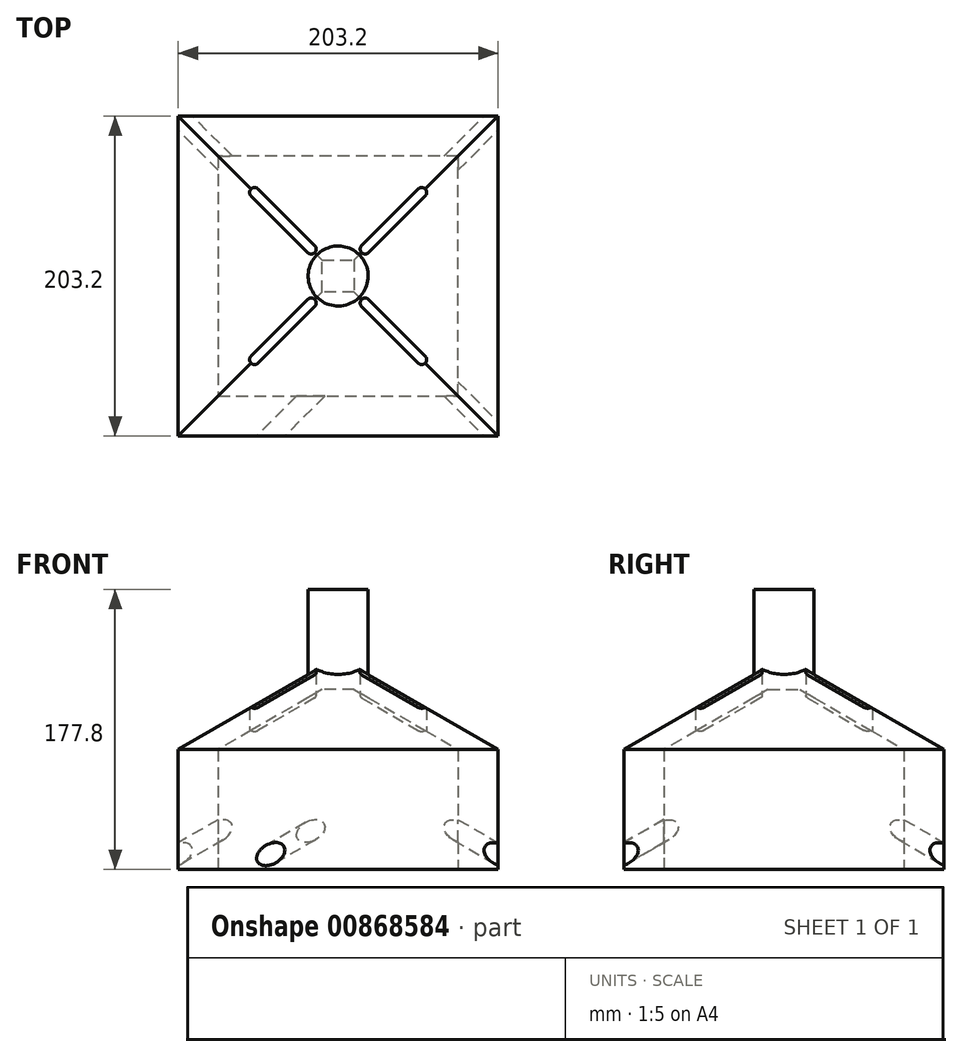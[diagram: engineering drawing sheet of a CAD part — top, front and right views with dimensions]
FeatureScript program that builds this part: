
annotation { "Feature Type Name" : "Feature", "Feature Type Description" : "" }
export const myFeature = defineFeature(function(context is Context, id is Id, definition is map)
    precondition{}
    {
        {
            var Q0;
            Q0=qCreatedBy(makeId("Top.planeOp"),FACE);
            var sketch = newSketch(context, id + "F0", { "sketchPlane" : qUnion([Q0])});
            skLineSegment(sketch, "E0.bottom", {"start": v(101.6, -101.6) * mm, "end": v(-101.6, -101.6) * mm});
            skLineSegment(sketch, "E0.top", {"start": v(101.6, 101.6) * mm, "end": v(-101.6, 101.6) * mm});
            skLineSegment(sketch, "E0.left", {"start": v(101.6, -101.6) * mm, "end": v(101.6, 101.6) * mm});
            skLineSegment(sketch, "E0.right", {"start": v(-101.6, -101.6) * mm, "end": v(-101.6, 101.6) * mm});
            skSolve(sketch);
        }
        {
            var Q0;
            Q0 = qSketchRegion(id + "F0", true);
            extrude(context, id + "F1", {"entities" : qUnion([Q0]), "depth" : 127 * mm, "offsetDistance" : 25.4 * mm});
        }
        {
            var Q0;
            Q0=makeQuery(id+"F0.imprint","IMPRINT",FACE,{"disambiguationData":[TD([[makeQuery(id+"F0.imprint","IMPRINT",EDGE,{"derivedFrom":sQuery(id+"F0.wireOp",EDGE,"E0.bottom")}),-1.0]])]});
            var sketch = newSketch(context, id + "F2", { "sketchPlane" : qUnion([Q0])});
            skLineSegment(sketch, "E1.0", {"start": v(76.2, -76.2) * mm, "end": v(76.2, 76.2) * mm});
            skLineSegment(sketch, "E1.1", {"start": v(-76.2, -76.2) * mm, "end": v(76.2, -76.2) * mm});
            skLineSegment(sketch, "E1.2", {"start": v(-76.2, 76.2) * mm, "end": v(-76.2, -76.2) * mm});
            skLineSegment(sketch, "E1.3", {"start": v(76.2, 76.2) * mm, "end": v(-76.2, 76.2) * mm});
            skSolve(sketch);
        }
        {
            var Q0;
            Q0 = qSketchRegion(id + "F2", true);
            extrude(context, id + "F3", {"entities" : qUnion([Q0]), "operationType" : NewBodyOperationType.REMOVE, "depth" : 76.2 * mm, "offsetDistance" : 25.4 * mm});
        }
        {
            var Q0;
            Q0=makeQuery(id+"F3.boolean.opBoolean","COPY",FACE,{"derivedFrom":makeQuery(id+"F3.opExtrude","CAP_FACE",FACE,{"disambiguationData":[OSD([sQuery(id+"F2.wireOp",EDGE,"E1.0"),sQuery(id+"F2.wireOp",EDGE,"E1.1"),sQuery(id+"F2.wireOp",EDGE,"E1.2"),sQuery(id+"F2.wireOp",EDGE,"E1.3")])],"isStart":false})});
            var sketch = newSketch(context, id + "F4", { "sketchPlane" : qUnion([Q0])});
            skLineSegment(sketch, "E2.0.0", {"start": v(76.2, -76.2) * mm, "end": v(76.2, 76.2) * mm});
            skLineSegment(sketch, "E2.0.1", {"start": v(76.2, 76.2) * mm, "end": v(-76.2, 76.2) * mm});
            skLineSegment(sketch, "E2.0.2", {"start": v(-76.2, 76.2) * mm, "end": v(-76.2, -76.2) * mm});
            skLineSegment(sketch, "E2.0.3", {"start": v(-76.2, -76.2) * mm, "end": v(76.2, -76.2) * mm});
            skSolve(sketch);
        }
        {
            var Q0;
            Q0 = qSketchRegion(id + "F4", true);
            extrude(context, id + "F5", {"entities" : qUnion([Q0]), "operationType" : NewBodyOperationType.REMOVE, "oppositeDirection" : true, "depth" : 101.6 * mm, "offsetDistance" : 25.4 * mm, "hasDraft" : true, "draftAngle" : 60 * degree, "draftPullDirection" : true});
        }
        {
            var Q0;
            Q0=makeQuery(id+"F1.opExtrude","CAP_EDGE",EDGE,{"disambiguationData":[OSD([sQuery(id+"F0.wireOp",EDGE,"E0.right")])],"isStart":false});
            var Q1;
            Q1=makeQuery(id+"F1.opExtrude","CAP_EDGE",EDGE,{"disambiguationData":[OSD([sQuery(id+"F0.wireOp",EDGE,"E0.top")])],"isStart":false});
            var Q2;
            Q2=makeQuery(id+"F1.opExtrude","CAP_EDGE",EDGE,{"disambiguationData":[OSD([sQuery(id+"F0.wireOp",EDGE,"E0.left")])],"isStart":false});
            var Q3;
            Q3=makeQuery(id+"F1.opExtrude","CAP_EDGE",EDGE,{"disambiguationData":[OSD([sQuery(id+"F0.wireOp",EDGE,"E0.bottom")])],"isStart":false});
            chamfer(context, id + "F6", {"entities" : qUnion([Q0, Q1, Q2, Q3]), "chamferType" : ChamferType.OFFSET_ANGLE, "width" : 50.8 * mm, "oppositeDirection" : false, "angle" : 60 * degree, "tangentPropagation" : true});
        }
        {
            var Q0;
            Q0=qCreatedBy(makeId("Top.planeOp"),FACE);
            var sketch = newSketch(context, id + "F7", { "sketchPlane" : qUnion([Q0])});
            skArc(sketch, "E3", {"start": v(-55.32, -50.82) * mm, "mid": v(-55.32, -55.32) * mm, "end": v(-50.82, -55.32) * mm});
            skArc(sketch, "E4", {"start": v(-14.9, -19.4) * mm, "mid": v(-14.9, -14.9) * mm, "end": v(-19.4, -14.9) * mm});
            skLineSegment(sketch, "E5", {"start": v(-50.82, -55.32) * mm, "end": v(-14.9, -19.4) * mm});
            skLineSegment(sketch, "E6", {"start": v(-55.32, -50.82) * mm, "end": v(-19.4, -14.9) * mm});
            skLineSegment(sketch, "E7", {"start": v(-55.32, -50.82) * mm, "end": v(-43.18, -62.96) * mm, "construction": true});
            skLineSegment(sketch, "E8", {"start": v(-25.58, -8.72) * mm, "end": v(-3.68, -30.62) * mm, "construction": true});
            skArc(sketch, "E9.1.0", {"start": v(-19.4, 14.9) * mm, "mid": v(-14.9, 14.9) * mm, "end": v(-14.9, 19.4) * mm});
            skLineSegment(sketch, "E9.1.1", {"start": v(-55.32, 50.82) * mm, "end": v(-19.4, 14.9) * mm});
            skLineSegment(sketch, "E9.1.2", {"start": v(-50.82, 55.32) * mm, "end": v(-14.9, 19.4) * mm});
            skArc(sketch, "E9.1.3", {"start": v(-50.82, 55.32) * mm, "mid": v(-55.32, 55.32) * mm, "end": v(-55.32, 50.82) * mm});
            skArc(sketch, "E9.2.0", {"start": v(14.9, 19.4) * mm, "mid": v(14.9, 14.9) * mm, "end": v(19.4, 14.9) * mm});
            skLineSegment(sketch, "E9.2.1", {"start": v(50.82, 55.32) * mm, "end": v(14.9, 19.4) * mm});
            skLineSegment(sketch, "E9.2.2", {"start": v(55.32, 50.82) * mm, "end": v(19.4, 14.9) * mm});
            skArc(sketch, "E9.2.3", {"start": v(55.32, 50.82) * mm, "mid": v(55.32, 55.32) * mm, "end": v(50.82, 55.32) * mm});
            skArc(sketch, "E9.3.0", {"start": v(19.4, -14.9) * mm, "mid": v(14.9, -14.9) * mm, "end": v(14.9, -19.4) * mm});
            skLineSegment(sketch, "E9.3.1", {"start": v(55.32, -50.82) * mm, "end": v(19.4, -14.9) * mm});
            skLineSegment(sketch, "E9.3.2", {"start": v(50.82, -55.32) * mm, "end": v(14.9, -19.4) * mm});
            skArc(sketch, "E9.3.3", {"start": v(50.82, -55.32) * mm, "mid": v(55.32, -55.32) * mm, "end": v(55.32, -50.82) * mm});
            skPoint(sketch, "E9.center", {"position": v(0, 0) * mm});
            skLineSegment(sketch, "E9.anchor1", {"start": v(0, 0) * mm, "end": v(-14.9, -19.4) * mm, "construction": true});
            skLineSegment(sketch, "E9.anchor2", {"start": v(0, 0) * mm, "end": v(19.4, -14.9) * mm, "construction": true});
            skSolve(sketch);
        }
        {
            var Q0;
            Q0 = qSketchRegion(id + "F7", true);
            var Q1;
            Q1=makeQuery(id+"F1.opExtrude","CAP_FACE",FACE,{"disambiguationData":[OSD([sQuery(id+"F0.wireOp",EDGE,"E0.bottom"),sQuery(id+"F0.wireOp",EDGE,"E0.top"),sQuery(id+"F0.wireOp",EDGE,"E0.left"),sQuery(id+"F0.wireOp",EDGE,"E0.right")])],"isStart":false});
            extrude(context, id + "F8", {"entities" : qUnion([Q0]), "operationType" : NewBodyOperationType.REMOVE, "endBound" : BoundingType.UP_TO_SURFACE, "depth" : 25.4 * mm, "endBoundEntityFace" : qUnion([Q1]), "offsetDistance" : 25.4 * mm});
        }
        {
            var Q0;
            Q0=makeQuery(id+"F1.opExtrude","CAP_VERTEX",VERTEX,{"disambiguationData":[OSD([sQuery(id+"F0.wireOp",EDGE,"E0.bottom"),sQuery(id+"F0.wireOp",EDGE,"E0.left")])],"isStart":true});
            var Q1;
            {var subQ0=sQuery(id+"F4.wireOp",EDGE,"E2.0.1");var subQ1=sQuery(id+"F4.wireOp",EDGE,"E2.0.0");Q1=makeQuery(id+"F8.boolean.opBoolean","SPLIT",EDGE,{"disambiguationData":[TD([makeQuery(id+"F3.boolean.opBoolean","COPY",FACE,{"derivedFrom":makeQuery(id+"F3.opExtrude","SWEPT_FACE",FACE,{"disambiguationData":[OSD([sQuery(id+"F2.wireOp",EDGE,"E1.0")])]})})])],"derivedFrom":makeQuery(id+"F5.boolean.opBoolean","COPY",EDGE,{"derivedFrom":makeQuery(id+"F5.opExtrude","SWEPT_EDGE",EDGE,{"disambiguationData":[OSD([subQ1,subQ0])]})})});}
            cPlane(context, id + "F9", {"entities" : qUnion([Q0, Q1]), "cplaneType" : CPlaneType.LINE_POINT, "offset" : 25.4 * mm, "width" : 152.4 * mm, "height" : 152.4 * mm});
        }
        {
            var Q0;
            Q0=qCreatedBy(id+"F9.planeOp",FACE);
            var sketch = newSketch(context, id + "F10", { "sketchPlane" : qUnion([Q0])});
            skCircle(sketch, "E10", {"center": v(22.34, 59.12) * mm, "radius": 6.35 * mm});
            skSolve(sketch);
        }
        {
            var Q0;
            Q0 = qSketchRegion(id + "F10", true);
            extrude(context, id + "F11", {"entities" : qUnion([Q0]), "operationType" : NewBodyOperationType.REMOVE, "oppositeDirection" : true, "depth" : 76.2 * mm, "offsetDistance" : 25.4 * mm});
        }
        {
            var Q0;
            Q0=makeQuery(id+"F1.opExtrude","CAP_VERTEX",VERTEX,{"disambiguationData":[OSD([sQuery(id+"F0.wireOp",EDGE,"E0.bottom"),sQuery(id+"F0.wireOp",EDGE,"E0.right")])],"isStart":true});
            var Q1;
            {var subQ0=sQuery(id+"F4.wireOp",EDGE,"E2.0.2");var subQ1=sQuery(id+"F4.wireOp",EDGE,"E2.0.1");Q1=makeQuery(id+"F8.boolean.opBoolean","SPLIT",EDGE,{"disambiguationData":[TD([makeQuery(id+"F3.boolean.opBoolean","COPY",FACE,{"derivedFrom":makeQuery(id+"F3.opExtrude","SWEPT_FACE",FACE,{"disambiguationData":[OSD([sQuery(id+"F2.wireOp",EDGE,"E1.1")])]})})])],"derivedFrom":makeQuery(id+"F5.boolean.opBoolean","COPY",EDGE,{"derivedFrom":makeQuery(id+"F5.opExtrude","SWEPT_EDGE",EDGE,{"disambiguationData":[OSD([subQ1,subQ0])]})})});}
            cPlane(context, id + "F12", {"entities" : qUnion([Q0, Q1]), "cplaneType" : CPlaneType.LINE_POINT, "offset" : 25.4 * mm, "width" : 152.4 * mm, "height" : 152.4 * mm});
        }
        {
            var Q0;
            Q0=makeQuery(id+"F1.opExtrude","CAP_VERTEX",VERTEX,{"disambiguationData":[OSD([sQuery(id+"F0.wireOp",EDGE,"E0.top"),sQuery(id+"F0.wireOp",EDGE,"E0.right")])],"isStart":true});
            var Q1;
            {var subQ0=sQuery(id+"F4.wireOp",EDGE,"E2.0.3");var subQ1=sQuery(id+"F4.wireOp",EDGE,"E2.0.2");Q1=makeQuery(id+"F8.boolean.opBoolean","SPLIT",EDGE,{"disambiguationData":[TD([makeQuery(id+"F5.boolean.opBoolean","COPY",FACE,{"derivedFrom":makeQuery(id+"F5.opExtrude","SWEPT_FACE",FACE,{"disambiguationData":[OSD([sQuery(id+"F4.wireOp",EDGE,"E2.0.0")])]})})])],"derivedFrom":makeQuery(id+"F5.boolean.opBoolean","COPY",EDGE,{"derivedFrom":makeQuery(id+"F5.opExtrude","SWEPT_EDGE",EDGE,{"disambiguationData":[OSD([subQ1,subQ0])]})})});}
            cPlane(context, id + "F13", {"entities" : qUnion([Q0, Q1]), "cplaneType" : CPlaneType.LINE_POINT, "offset" : 25.4 * mm, "width" : 152.4 * mm, "height" : 152.4 * mm});
        }
        {
            var Q0;
            Q0=makeQuery(id+"F1.opExtrude","CAP_VERTEX",VERTEX,{"disambiguationData":[OSD([sQuery(id+"F0.wireOp",EDGE,"E0.top"),sQuery(id+"F0.wireOp",EDGE,"E0.left")])],"isStart":true});
            var Q1;
            {var subQ0=sQuery(id+"F4.wireOp",EDGE,"E2.0.3");var subQ1=sQuery(id+"F4.wireOp",EDGE,"E2.0.0");Q1=makeQuery(id+"F8.boolean.opBoolean","SPLIT",EDGE,{"disambiguationData":[TD([makeQuery(id+"F5.boolean.opBoolean","COPY",FACE,{"derivedFrom":makeQuery(id+"F5.opExtrude","SWEPT_FACE",FACE,{"disambiguationData":[OSD([sQuery(id+"F4.wireOp",EDGE,"E2.0.1")])]})})])],"derivedFrom":makeQuery(id+"F5.boolean.opBoolean","COPY",EDGE,{"derivedFrom":makeQuery(id+"F5.opExtrude","SWEPT_EDGE",EDGE,{"disambiguationData":[OSD([subQ1,subQ0])]})})});}
            cPlane(context, id + "F14", {"entities" : qUnion([Q0, Q1]), "cplaneType" : CPlaneType.LINE_POINT, "offset" : 25.4 * mm, "width" : 152.4 * mm, "height" : 152.4 * mm});
        }
        {
            var Q0;
            Q0=qCreatedBy(id+"F12.planeOp",FACE);
            var sketch = newSketch(context, id + "F15", { "sketchPlane" : qUnion([Q0])});
            skCircle(sketch, "E11", {"center": v(22.05, 59.22) * mm, "radius": 6.35 * mm});
            skSolve(sketch);
        }
        {
            var Q0;
            Q0 = qSketchRegion(id + "F15", true);
            extrude(context, id + "F16", {"entities" : qUnion([Q0]), "operationType" : NewBodyOperationType.REMOVE, "oppositeDirection" : true, "depth" : 127 * mm, "offsetDistance" : 25.4 * mm});
        }
        {
            var Q0;
            Q0=qCreatedBy(id+"F13.planeOp",FACE);
            var sketch = newSketch(context, id + "F17", { "sketchPlane" : qUnion([Q0])});
            skCircle(sketch, "E12", {"center": v(22.34, 59.12) * mm, "radius": 6.35 * mm});
            skSolve(sketch);
        }
        {
            var Q0;
            Q0 = qSketchRegion(id + "F17", true);
            extrude(context, id + "F18", {"entities" : qUnion([Q0]), "operationType" : NewBodyOperationType.REMOVE, "oppositeDirection" : true, "depth" : 127 * mm, "offsetDistance" : 25.4 * mm});
        }
        {
            var Q0;
            Q0=qCreatedBy(id+"F14.planeOp",FACE);
            var sketch = newSketch(context, id + "F19", { "sketchPlane" : qUnion([Q0])});
            skCircle(sketch, "E13", {"center": v(-22.34, 59.12) * mm, "radius": 6.35 * mm});
            skSolve(sketch);
        }
        {
            var Q0;
            Q0 = qSketchRegion(id + "F19", true);
            extrude(context, id + "F20", {"entities" : qUnion([Q0]), "operationType" : NewBodyOperationType.REMOVE, "oppositeDirection" : true, "depth" : 127 * mm, "offsetDistance" : 25.4 * mm});
        }
        {
            var Q0;
            Q0=makeQuery(id+"F1.opExtrude","CAP_FACE",FACE,{"disambiguationData":[OSD([sQuery(id+"F0.wireOp",EDGE,"E0.bottom"),sQuery(id+"F0.wireOp",EDGE,"E0.top"),sQuery(id+"F0.wireOp",EDGE,"E0.left"),sQuery(id+"F0.wireOp",EDGE,"E0.right")])],"isStart":false});
            var sketch = newSketch(context, id + "F21", { "sketchPlane" : qUnion([Q0])});
            skCircle(sketch, "E14", {"center": v(0, 0) * mm, "radius": 19.05 * mm});
            skSolve(sketch);
        }
        {
            var Q0;
            Q0 = qSketchRegion(id + "F21", true);
            extrude(context, id + "F22", {"entities" : qUnion([Q0]), "operationType" : NewBodyOperationType.ADD, "depth" : 50.8 * mm, "offsetDistance" : 25.4 * mm, "hasSecondDirection" : true, "secondDirectionOppositeDirection" : true, "secondDirectionDepth" : 12.7 * mm});
        }
    });
